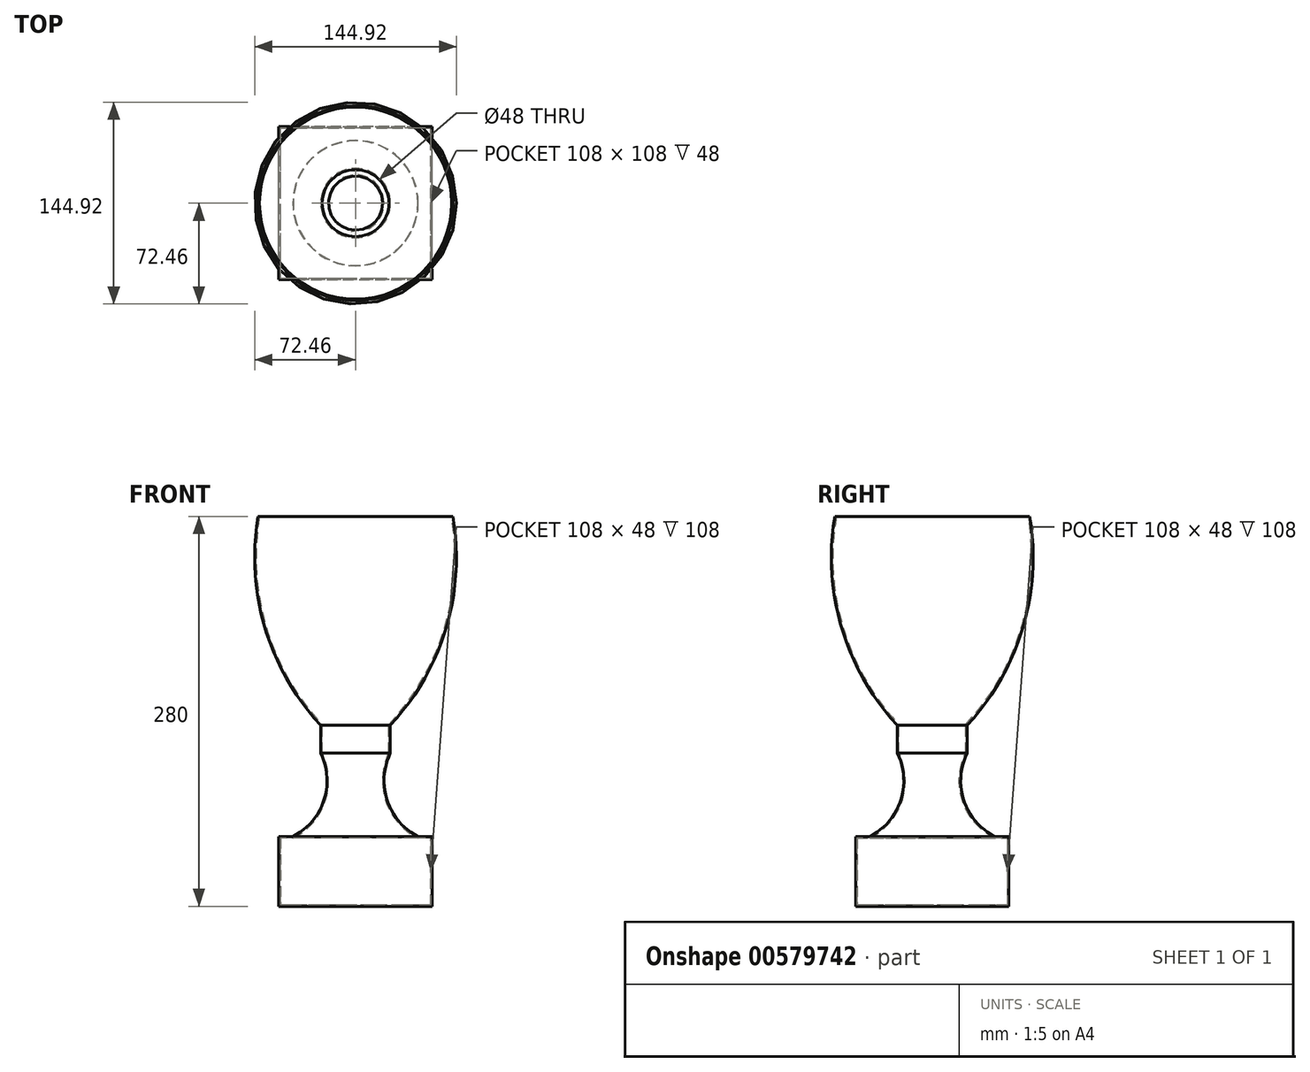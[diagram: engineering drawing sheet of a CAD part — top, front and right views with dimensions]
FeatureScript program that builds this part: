
annotation { "Feature Type Name" : "Feature", "Feature Type Description" : "" }
export const myFeature = defineFeature(function(context is Context, id is Id, definition is map)
    precondition{}
    {
        {
            var Q0;
            Q0=qCreatedBy(makeId("Front.planeOp"),FACE);
            var sketch = newSketch(context, id + "F0", { "sketchPlane" : qUnion([Q0])});
            skLineSegment(sketch, "E0", {"start": v(55, 50) * mm, "end": v(100, 50) * mm});
            skLineSegment(sketch, "E1", {"start": v(55, 130) * mm, "end": v(80, 130) * mm});
            skLineSegment(sketch, "E2", {"start": v(80, 130) * mm, "end": v(80, 110) * mm});
            skLineSegment(sketch, "E3", {"start": v(80, 110) * mm, "end": v(55, 110) * mm});
            skArc(sketch, "E4", {"start": v(80, 110) * mm, "mid": v(77.77, 75.92) * mm, "end": v(100, 50) * mm});
            skLineSegment(sketch, "E5", {"start": v(55, 130) * mm, "end": v(55, 50) * mm});
            skSolve(sketch);
        }
        {
            var Q0;
            Q0=qCreatedBy(makeId("Front.planeOp"),FACE);
            var sketch = newSketch(context, id + "F1", { "sketchPlane" : qUnion([Q0])});
            skLineSegment(sketch, "E6", {"start": v(0, 0) * mm, "end": v(110, 0) * mm});
            skLineSegment(sketch, "E7", {"start": v(110, 0) * mm, "end": v(110, 50) * mm});
            skLineSegment(sketch, "E8", {"start": v(110, 50) * mm, "end": v(0, 50) * mm});
            skLineSegment(sketch, "E9", {"start": v(0, 50) * mm, "end": v(0, 0) * mm});
            skSolve(sketch);
        }
        {
            var Q0;
            Q0 = qSketchRegion(id + "F1", true);
            extrude(context, id + "F2", {"entities" : qUnion([Q0]), "endBound" : BoundingType.SYMMETRIC, "depth" : 110 * mm, "offsetDistance" : 25 * mm});
        }
        {
            var Q0;
            Q0=qCreatedBy(makeId("Front.planeOp"),FACE);
            var sketch = newSketch(context, id + "F3", { "sketchPlane" : qUnion([Q0])});
            skLineSegment(sketch, "E10", {"start": v(0, 0) * mm, "end": v(55, 0) * mm});
            skLineSegment(sketch, "E11", {"start": v(55, 130) * mm, "end": v(55, 280) * mm});
            skLineSegment(sketch, "E12", {"start": v(55, 280) * mm, "end": v(125, 280) * mm});
            skLineSegment(sketch, "E13", {"start": v(55, 130) * mm, "end": v(80, 130) * mm});
            skArc(sketch, "E14", {"start": v(80, 130) * mm, "mid": v(120, 199.75) * mm, "end": v(125, 280) * mm});
            skSolve(sketch);
        }
        {
            var Q0;
            Q0 = qSketchRegion(id + "F0", true);
            var Q1;
            Q1=sQuery(id+"F0.wireOp",EDGE,"E5");
            revolve(context, id + "F4", {"operationType" : NewBodyOperationType.ADD, "entities" : qUnion([Q0]), "axis" : qUnion([Q1]), "revolveType" : RevolveType.FULL});
        }
        {
            var Q0;
            Q0 = qSketchRegion(id + "F3", true);
            var Q1;
            Q1=sQuery(id+"F3.wireOp",EDGE,"E11");
            revolve(context, id + "F5", {"operationType" : NewBodyOperationType.ADD, "entities" : qUnion([Q0]), "axis" : qUnion([Q1]), "revolveType" : RevolveType.FULL});
        }
        {
            var Q0;
            Q0=makeQuery(id+"F5.opRevolve","SWEPT_FACE",FACE,{"disambiguationData":[OSD([sQuery(id+"F3.wireOp",EDGE,"E12")])]});
            shell(context, id + "F6", {"entities" : qUnion([Q0]), "thickness" : 1 * mm});
        }
    });
